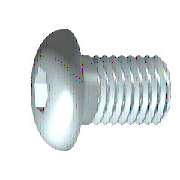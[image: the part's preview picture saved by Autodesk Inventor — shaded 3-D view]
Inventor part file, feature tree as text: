
AUTODESK INVENTOR PART (.ipt)
format: ipt  version: 2018 (Build 220112000, 112)  size: 199,680 bytes
history: native  units: mm (DEFAULTED — no unit token found)
features: sketch x2, extrude x1, plane x1, fillet x1
ambient origin geometry x7: Origin, YZ Plane, XY Plane, X Axis, Y Axis, Z Axis, Center Point
bodies: Solid1 (feature_tree), Body (feature_tree)
feature tree (5):
  extrude  "Slot"  Depth=1.8542mm
  plane  "Work Plane1"
  fillet  "Fillet2"  Radius=1.8542mm
  sketch  "Sketch1"  dims[d1=4.75976mm d2=1.59014mm d3=1.8542mm]
  sketch  "Sketch2"  dims[d4=1.1176mm d5=60.0deg d6=3.5052mm d7=3.5052mm d8=2.287693mm d9=6.6548mm d10=90.0deg d11=10.0mm d12=0.0mm d13=4.75976mm d14=0.0mm d15=0.486918mm d16=0.486918mm d17=1.6002mm d19=0.0mm d26=6.35mm d27=45.0deg d28=0.0mm d29=0.0mm d30=0.1mm]
